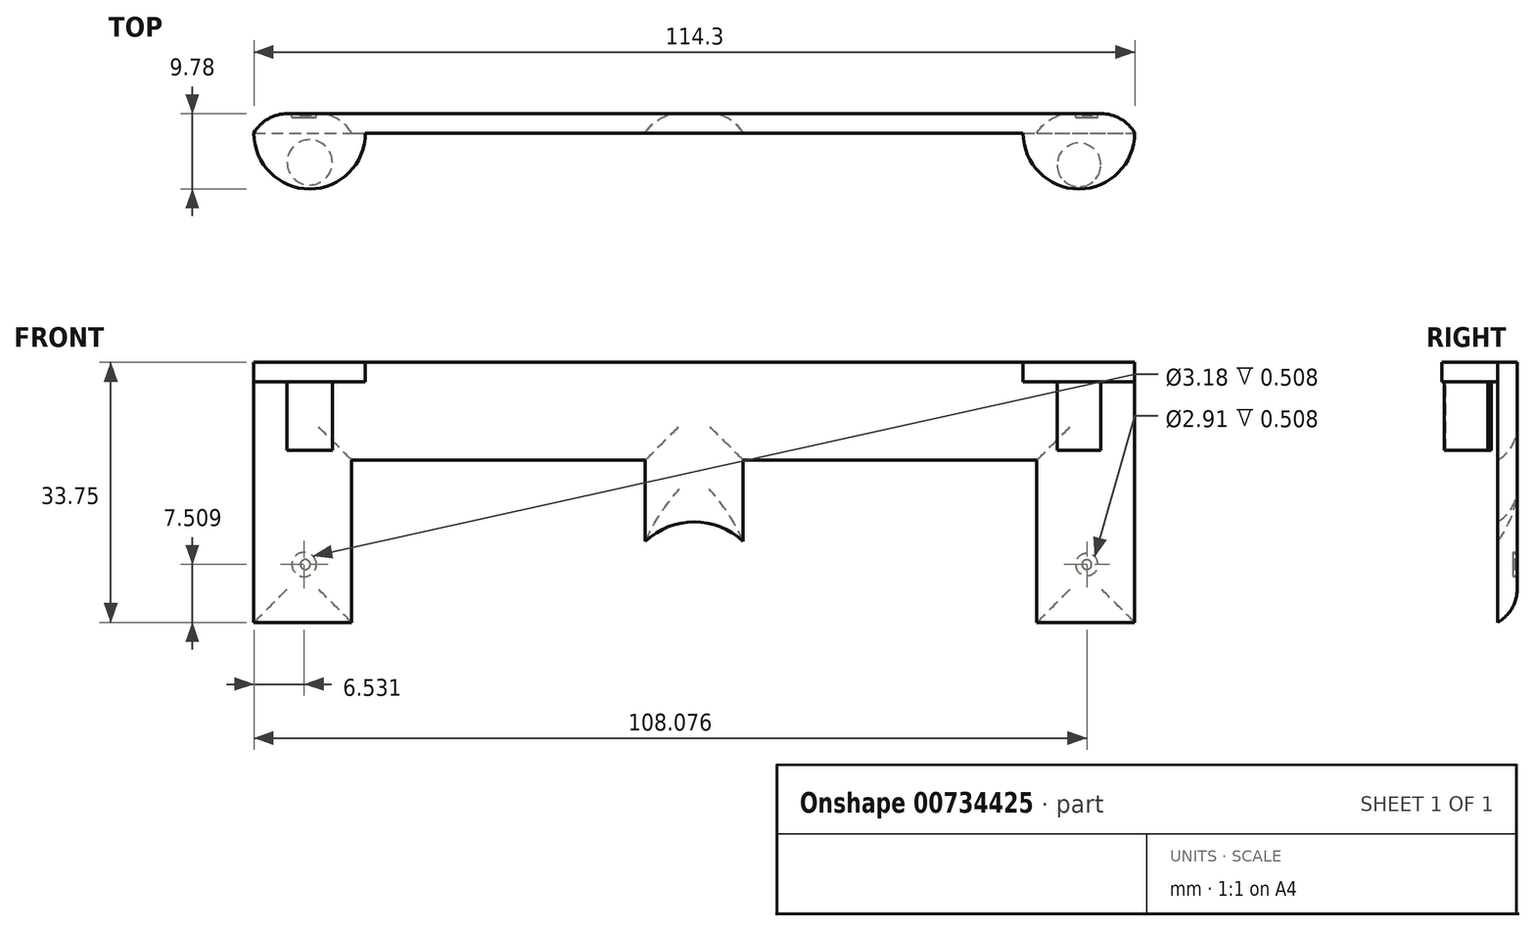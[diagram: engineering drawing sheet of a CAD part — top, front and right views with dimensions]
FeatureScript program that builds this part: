
annotation { "Feature Type Name" : "Feature", "Feature Type Description" : "" }
export const myFeature = defineFeature(function(context is Context, id is Id, definition is map)
    precondition{}
    {
        {
            var Q0;
            Q0=qCreatedBy(makeId("Front.planeOp"),FACE);
            var sketch = newSketch(context, id + "F0", { "sketchPlane" : qUnion([Q0])});
            skLineSegment(sketch, "E0", {"start": v(-86.75, 41.77) * mm, "end": v(-86.75, 8.02) * mm});
            skLineSegment(sketch, "E1", {"start": v(-86.75, 8.02) * mm, "end": v(-74.05, 8.02) * mm});
            skLineSegment(sketch, "E2", {"start": v(-74.05, 8.02) * mm, "end": v(-74.05, 29.07) * mm});
            skLineSegment(sketch, "E3", {"start": v(-74.05, 29.07) * mm, "end": v(-35.95, 29.07) * mm});
            skLineSegment(sketch, "E4", {"start": v(-35.95, 29.07) * mm, "end": v(-35.95, 8.02) * mm});
            skLineSegment(sketch, "E5", {"start": v(-35.95, 8.02) * mm, "end": v(-23.25, 8.02) * mm});
            skLineSegment(sketch, "E6", {"start": v(-23.25, 8.02) * mm, "end": v(-23.25, 29.07) * mm});
            skLineSegment(sketch, "E7", {"start": v(-23.25, 29.07) * mm, "end": v(14.85, 29.07) * mm});
            skLineSegment(sketch, "E8", {"start": v(14.85, 29.07) * mm, "end": v(14.85, 8.02) * mm});
            skLineSegment(sketch, "E9", {"start": v(14.85, 8.02) * mm, "end": v(27.55, 8.02) * mm});
            skLineSegment(sketch, "E10", {"start": v(27.55, 8.02) * mm, "end": v(27.55, 41.77) * mm});
            skLineSegment(sketch, "E11", {"start": v(-86.75, 41.77) * mm, "end": v(27.55, 41.77) * mm});
            skSolve(sketch);
        }
        {
            var Q0;
            Q0=makeQuery(id+"F0.imprint","IMPRINT",FACE,{"disambiguationData":[TD([[makeQuery(id+"F0.imprint","IMPRINT",EDGE,{"derivedFrom":sQuery(id+"F0.wireOp",EDGE,"E0")}),1.0]])]});
            extrude(context, id + "F1", {"entities" : qUnion([Q0]), "depth" : 2.54 * mm, "offsetDistance" : 25.4 * mm});
        }
        {
            var Q0;
            Q0=makeQuery(id+"F1.opExtrude","SWEPT_FACE",FACE,{"disambiguationData":[OSD([sQuery(id+"F0.wireOp",EDGE,"E11")])]});
            var sketch = newSketch(context, id + "F2", { "sketchPlane" : qUnion([Q0])});
            skArc(sketch, "E12", {"start": v(-86.75, -2.54) * mm, "mid": v(-79.51, -9.78) * mm, "end": v(-72.28, -2.54) * mm});
            skArc(sketch, "E13", {"start": v(13.07, -2.54) * mm, "mid": v(20.3, -9.78) * mm, "end": v(27.55, -2.54) * mm});
            skSolve(sketch);
        }
        {
            var Q0;
            {var subQ0=sQuery(id+"F2.wireOp",EDGE,"E13");Q0=makeQuery(id+"F2.imprint","IMPRINT",FACE,{"disambiguationData":[TD([[makeQuery(id+"F2.imprint","IMPRINT",EDGE,{"derivedFrom":subQ0}),1.0]])]});}
            var Q1;
            {var subQ0=sQuery(id+"F2.wireOp",EDGE,"E12");Q1=makeQuery(id+"F2.imprint","IMPRINT",FACE,{"disambiguationData":[TD([[makeQuery(id+"F2.imprint","IMPRINT",EDGE,{"derivedFrom":subQ0}),1.0]])]});}
            extrude(context, id + "F3", {"entities" : qUnion([Q0, Q1]), "operationType" : NewBodyOperationType.ADD, "oppositeDirection" : true, "depth" : 2.54 * mm, "offsetDistance" : 25.4 * mm});
        }
        {
            var Q0;
            Q0=makeQuery(id+"F3.opExtrude","CAP_FACE",FACE,{"disambiguationData":[OSD([sQuery(id+"F0.wireOp",EDGE,"E11"),sQuery(id+"F2.wireOp",EDGE,"E12")])],"isStart":false});
            var sketch = newSketch(context, id + "F4", { "sketchPlane" : qUnion([Q0])});
            skCircle(sketch, "E14", {"center": v(-79.51, 6.33) * mm, "radius": 2.93 * mm});
            skPoint(sketch, "E14.centerSnap0", {"position": v(-79.51, 2.54) * mm});
            skSolve(sketch);
        }
        {
            var Q0;
            Q0=makeQuery(id+"F3.opExtrude","CAP_FACE",FACE,{"disambiguationData":[OSD([sQuery(id+"F0.wireOp",EDGE,"E11"),sQuery(id+"F2.wireOp",EDGE,"E13")])],"isStart":false});
            var sketch = newSketch(context, id + "F5", { "sketchPlane" : qUnion([Q0])});
            skCircle(sketch, "E15", {"center": v(20.3, 6.66) * mm, "radius": 2.83 * mm});
            skPoint(sketch, "E15.centerSnap0", {"position": v(20.3, 2.54) * mm});
            skSolve(sketch);
        }
        {
            var Q0;
            Q0=makeQuery(id+"F4.imprint","IMPRINT",FACE,{"disambiguationData":[TD([[makeQuery(id+"F4.imprint","IMPRINT",EDGE,{"derivedFrom":sQuery(id+"F4.wireOp",EDGE,"E14")}),1.0]])]});
            var Q1;
            Q1=makeQuery(id+"F5.imprint","IMPRINT",FACE,{"disambiguationData":[TD([[makeQuery(id+"F5.imprint","IMPRINT",EDGE,{"derivedFrom":sQuery(id+"F5.wireOp",EDGE,"E15")}),1.0]])]});
            extrude(context, id + "F6", {"entities" : qUnion([Q0, Q1]), "operationType" : NewBodyOperationType.ADD, "depth" : 8.9 * mm, "offsetDistance" : 25.4 * mm});
        }
        {
            var Q0;
            Q0=makeQuery(id+"F1.opExtrude","CAP_FACE",FACE,{"disambiguationData":[OSD([sQuery(id+"F0.wireOp",EDGE,"E0"),sQuery(id+"F0.wireOp",EDGE,"E1"),sQuery(id+"F0.wireOp",EDGE,"E2"),sQuery(id+"F0.wireOp",EDGE,"E3"),sQuery(id+"F0.wireOp",EDGE,"E4"),sQuery(id+"F0.wireOp",EDGE,"E5"),sQuery(id+"F0.wireOp",EDGE,"E6"),sQuery(id+"F0.wireOp",EDGE,"E7"),sQuery(id+"F0.wireOp",EDGE,"E8"),sQuery(id+"F0.wireOp",EDGE,"E9"),sQuery(id+"F0.wireOp",EDGE,"E10"),sQuery(id+"F0.wireOp",EDGE,"E11")])],"isStart":false});
            var sketch = newSketch(context, id + "F7", { "sketchPlane" : qUnion([Q0])});
            skArc(sketch, "E16", {"start": v(-23.25, 18.55) * mm, "mid": v(-29.6, 21.07) * mm, "end": v(-35.95, 18.55) * mm});
            skSolve(sketch);
        }
        {
            var Q0;
            {var subQ0=sQuery(id+"F7.wireOp",EDGE,"E16");Q0=makeQuery(id+"F7.imprint","IMPRINT",FACE,{"disambiguationData":[TD([[makeQuery(id+"F7.imprint","IMPRINT",EDGE,{"derivedFrom":subQ0}),1.0]])]});}
            extrude(context, id + "F8", {"entities" : qUnion([Q0]), "operationType" : NewBodyOperationType.REMOVE, "oppositeDirection" : true, "depth" : 25.4 * mm, "offsetDistance" : 25.4 * mm});
        }
        {
            var Q0;
            Q0=makeQuery(id+"F1.opExtrude","CAP_EDGE",EDGE,{"disambiguationData":[OSD([sQuery(id+"F0.wireOp",EDGE,"E7")])],"isStart":true});
            var Q1;
            Q1=makeQuery(id+"F1.opExtrude","CAP_EDGE",EDGE,{"disambiguationData":[OSD([sQuery(id+"F0.wireOp",EDGE,"E3")])],"isStart":true});
            var Q2;
            Q2=makeQuery(id+"F8.boolean.opBoolean","INTERSECT",EDGE,{"derivedFrom":[makeQuery(id+"F1.opExtrude","CAP_FACE",FACE,{"disambiguationData":[OSD([sQuery(id+"F0.wireOp",EDGE,"E0"),sQuery(id+"F0.wireOp",EDGE,"E1"),sQuery(id+"F0.wireOp",EDGE,"E2"),sQuery(id+"F0.wireOp",EDGE,"E3"),sQuery(id+"F0.wireOp",EDGE,"E4"),sQuery(id+"F0.wireOp",EDGE,"E5"),sQuery(id+"F0.wireOp",EDGE,"E6"),sQuery(id+"F0.wireOp",EDGE,"E7"),sQuery(id+"F0.wireOp",EDGE,"E8"),sQuery(id+"F0.wireOp",EDGE,"E9"),sQuery(id+"F0.wireOp",EDGE,"E10"),sQuery(id+"F0.wireOp",EDGE,"E11")])],"isStart":true}),makeQuery(id+"F8.opExtrude","SWEPT_FACE",FACE,{"disambiguationData":[OSD([sQuery(id+"F7.wireOp",EDGE,"E16")])]})]});
            var Q3;
            Q3=makeQuery(id+"F1.opExtrude","CAP_EDGE",EDGE,{"disambiguationData":[OSD([sQuery(id+"F0.wireOp",EDGE,"E4")])],"isStart":true});
            var Q4;
            Q4=makeQuery(id+"F1.opExtrude","CAP_EDGE",EDGE,{"disambiguationData":[OSD([sQuery(id+"F0.wireOp",EDGE,"E6")])],"isStart":true});
            var Q5;
            Q5=makeQuery(id+"F1.opExtrude","CAP_EDGE",EDGE,{"disambiguationData":[OSD([sQuery(id+"F0.wireOp",EDGE,"E8")])],"isStart":true});
            var Q6;
            Q6=makeQuery(id+"F1.opExtrude","CAP_EDGE",EDGE,{"disambiguationData":[OSD([sQuery(id+"F0.wireOp",EDGE,"E10")])],"isStart":true});
            var Q7;
            Q7=makeQuery(id+"F1.opExtrude","CAP_EDGE",EDGE,{"disambiguationData":[OSD([sQuery(id+"F0.wireOp",EDGE,"E1")])],"isStart":true});
            var Q8;
            Q8=makeQuery(id+"F1.opExtrude","CAP_EDGE",EDGE,{"disambiguationData":[OSD([sQuery(id+"F0.wireOp",EDGE,"E2")])],"isStart":true});
            var Q9;
            Q9=makeQuery(id+"F1.opExtrude","CAP_EDGE",EDGE,{"disambiguationData":[OSD([sQuery(id+"F0.wireOp",EDGE,"E0")])],"isStart":true});
            var Q10;
            Q10=makeQuery(id+"F1.opExtrude","CAP_EDGE",EDGE,{"disambiguationData":[OSD([sQuery(id+"F0.wireOp",EDGE,"E9")])],"isStart":true});
            fillet(context, id + "F9", {"entities" : qUnion([Q0, Q1, Q2, Q3, Q4, Q5, Q6, Q7, Q8, Q9, Q10]), "radius" : 5.08 * mm, "tangentPropagation" : true, "allowEdgeOverflow" : false});
        }
        {
            var Q0;
            Q0=qCreatedBy(makeId("Front.planeOp"),FACE);
            var sketch = newSketch(context, id + "F10", { "sketchPlane" : qUnion([Q0])});
            skCircle(sketch, "E17", {"center": v(21.33, 15.53) * mm, "radius": 1.46 * mm});
            skCircle(sketch, "E18", {"center": v(-80.22, 15.53) * mm, "radius": 1.59 * mm});
            skSolve(sketch);
        }
        {
            var Q0;
            Q0 = qSketchRegion(id + "F10", true);
            extrude(context, id + "F11", {"entities" : qUnion([Q0]), "operationType" : NewBodyOperationType.REMOVE, "depth" : 0.5 * mm, "offsetDistance" : 25.4 * mm});
        }
        {
            var Q0;
            Q0=makeQuery(id+"F11.boolean.opBoolean","COPY",FACE,{"derivedFrom":makeQuery(id+"F11.opExtrude","CAP_FACE",FACE,{"disambiguationData":[OSD([sQuery(id+"F10.wireOp",EDGE,"E17")])],"isStart":false})});
            var sketch = newSketch(context, id + "F12", { "sketchPlane" : qUnion([Q0])});
            skCircle(sketch, "E19", {"center": v(-21.33, 15.53) * mm, "radius": 0.62 * mm});
            skCircle(sketch, "E20", {"center": v(80.08, 15.53) * mm, "radius": 0.65 * mm});
            skSolve(sketch);
        }
        {
            var Q0;
            Q0 = qSketchRegion(id + "F12", true);
            extrude(context, id + "F13", {"entities" : qUnion([Q0]), "operationType" : NewBodyOperationType.ADD, "depth" : 0.25 * mm, "offsetDistance" : 25.4 * mm});
        }
    });
